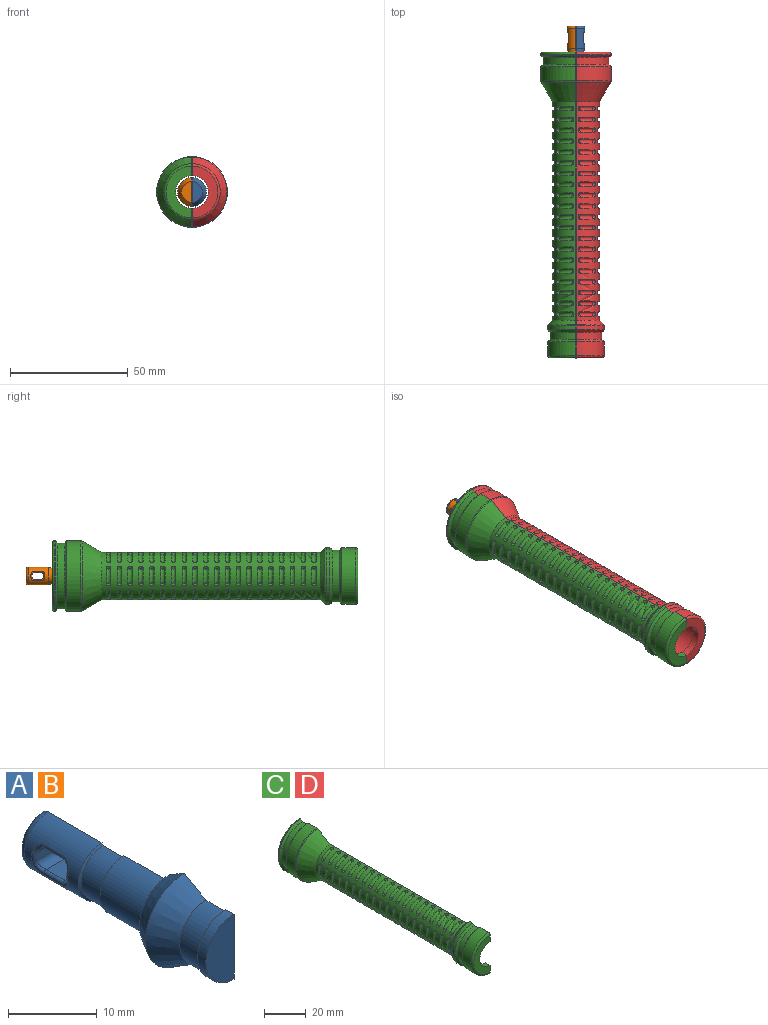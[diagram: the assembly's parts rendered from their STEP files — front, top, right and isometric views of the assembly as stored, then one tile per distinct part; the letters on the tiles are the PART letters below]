
ASSEMBLY  parts=4 mates=3
PART A: 31 faces, bbox 6.2x30.6x12.3 mm
  f0: cone r=3.5mm half-angle=60deg, axis (0,1,0), area 4mm2, adj f1,f12,f13
  f1: cylinder r=3.5mm len=7mm, axis (0,1,0), area 34.4mm2, adj f0,f2,f13
  f2: cone r=3.8mm half-angle=60deg, axis (0,-1,0), area 4mm2, adj f1,f3,f13
  f3: cylinder r=3.8mm len=7.6mm, axis (0,1,0), area 87mm2, adj f2,f4,f13
  f4: plane 9.6x4.8mm, normal (0,1,0), area 13.5mm2, adj f3,f5,f13
  f5: cone r=4.8mm half-angle=30deg, axis (0,-1,0), area 46.7mm2, adj f4,f6,f13
  f6: cone r=6.16mm half-angle=30deg, axis (0,1,0), area 64.5mm2, adj f5,f7,f13
  f7: cylinder r=4.17mm len=8.34mm, axis (0,1,0), area 39.3mm2, adj f6,f8,f13
  f8: cone r=4.17mm half-angle=60deg, axis (0,-1,0), area 4.9mm2, adj f7,f9,f13
  f9: cylinder r=4.48mm len=8.97mm, axis (0,1,0), area 18.3mm2, adj f8,f10,f13
  f10: plane 8.97x4.48mm, normal (0,-1,0), area 31.6mm2, adj f9,f13
  f11: plane 5.6x2.8mm, normal (0,1,0), area 12.3mm2, adj f13,f14
  f12: cylinder r=3.8mm len=8.54mm, axis (0,1,0), area 78mm2, adj f0,f13,f14,f23,f24,f25,f26,f27
  f13: plane 30.58x12.32mm, normal (1,0,0), area 237.3mm2, adj f0,f1,f2,f3,f4,f5,f6,f7
  f14: torus R=2.8mm, axis (0,1,0), area 17mm2, adj f11,f12,f13
  f15: plane 3.4x1mm, normal (0,-1,0), area 3.4mm2, adj f13,f19,f22,f27
  f16: plane 3x2.82mm, normal (0,0,-1), area 8.5mm2, adj f13,f19,f20,f30
  f17: plane 3.4x1mm, normal (0,1,0), area 3.4mm2, adj f13,f20,f21,f26
  f18: plane 3x2.82mm, normal (0,0,1), area 8.5mm2, adj f13,f21,f22,f23
  f19: cylinder r=1mm len=3.36mm, axis (-1,0,0), area 4.8mm2, adj f13,f15,f16,f29
  f20: cylinder r=1mm len=3.36mm, axis (1,0,0), area 4.8mm2, adj f13,f16,f17,f28
  f21: cylinder r=1mm len=3.36mm, axis (-1,0,0), area 4.8mm2, adj f13,f17,f18,f24
  f22: cylinder r=1mm len=3.36mm, axis (1,0,0), area 4.8mm2, adj f13,f15,f18,f25
  f23: cylinder r=0.4mm len=3mm, axis (0,1,0), area 2.6mm2, adj f12,f18,f24,f25
  f24: bspline ~1.89x1.68mm, area 1.4mm2, adj f12,f21,f23,f26
  f25: bspline ~1.89x1.68mm, area 1.4mm2, adj f12,f22,f23,f27
  f26: torus R=3.4mm, axis (0,1,0), area 0.7mm2, adj f12,f17,f24,f28
  f27: torus R=3.4mm, axis (0,1,0), area 0.7mm2, adj f12,f15,f25,f29
  f28: bspline ~1.89x1.68mm, area 1.4mm2, adj f12,f20,f26,f30
  f29: bspline ~1.89x1.68mm, area 1.4mm2, adj f12,f19,f27,f30
  f30: cylinder r=0.4mm len=3mm, axis (0,1,0), area 2.6mm2, adj f12,f16,f28,f29
PART B: same geometry as A
PART C: 333 faces, bbox 16.2x130x32.5 mm
  f0: cylinder r=14mm len=28mm, axis (0,1,0), area 131.9mm2, adj f1,f25,f26,f27
  f1: cone r=14mm half-angle=45deg, axis (0,-1,0), area 64.4mm2, adj f0,f2,f26,f27
  f2: cylinder r=15mm len=30mm, axis (0,1,0), area 281.9mm2, adj f1,f26,f27,f328
  f3: cone r=15mm half-angle=30deg, axis (0,1,0), area 380.1mm2, adj f4,f26,f27,f328
  f4: cylinder r=10mm len=92.84mm, axis (0,1,0), area 1921mm2, adj f3,f5,f26,f27,f28,f29,f31,f33
  f5: cone r=12mm half-angle=45deg, axis (0,-1,0), area 82.3mm2, adj f4,f26,f27,f329
  f6: cylinder r=12mm len=24mm, axis (0,1,0), area 63.8mm2, adj f7,f26,f27,f329
  f7: cone r=12mm half-angle=45deg, axis (0,1,0), area 51.1mm2, adj f6,f8,f26,f27
  f8: cylinder r=11mm len=22mm, axis (0,1,0), area 103.7mm2, adj f7,f9,f26,f27
  f9: cone r=11mm half-angle=45deg, axis (0,-1,0), area 51.1mm2, adj f8,f10,f26,f27
  f10: cylinder r=12mm len=24mm, axis (0,1,0), area 222.2mm2, adj f9,f26,f27,f330
  f11: plane 22x11mm, normal (0,-1,0), area 113.1mm2, adj f12,f26,f27,f330
  f12: cylinder r=7mm len=14mm, axis (0,1,0), area 66mm2, adj f11,f13,f26,f27
  f13: plane 18x9mm, normal (0,1,0), area 50.3mm2, adj f12,f14,f26,f27
  f14: cylinder r=9mm len=18mm, axis (0,1,0), area 275.9mm2, adj f13,f15,f26,f27
  f15: cone r=7mm half-angle=45deg, axis (0,-1,0), area 71.1mm2, adj f14,f16,f26,f27
  f16: cylinder r=7mm len=94.33mm, axis (0,1,0), area 2074.4mm2, adj f15,f17,f26,f27
  f17: cone r=10.2mm half-angle=19deg, axis (0,1,0), area 266.1mm2, adj f16,f18,f26,f27
  f18: cylinder r=10.2mm len=20.4mm, axis (0,1,0), area 80.1mm2, adj f17,f19,f26,f27
  f19: plane 22.4x11.2mm, normal (0,1,0), area 33.6mm2, adj f18,f20,f26,f27
  f20: cylinder r=11.2mm len=22.4mm, axis (0,1,0), area 249.8mm2, adj f19,f21,f26,f27
  f21: plane 22.4x11.2mm, normal (0,-1,0), area 33.6mm2, adj f20,f22,f26,f27
  f22: cylinder r=10.2mm len=20.4mm, axis (0,1,0), area 32mm2, adj f21,f26,f27,f331
  f23: plane 28x14mm, normal (0,1,0), area 110.8mm2, adj f26,f27,f331,f332
  f24: cylinder r=15mm len=30mm, axis (0,1,0), area 11.8mm2, adj f25,f26,f27,f332
  f25: cone r=15mm half-angle=45deg, axis (0,1,0), area 64.4mm2, adj f0,f24,f26,f27
  f26: plane 130x8mm, normal (1,0,0), area 414.8mm2, adj f0,f1,f2,f3,f4,f5,f6,f7
  f27: plane 130x8mm, normal (1,0,0), area 414.8mm2, adj f0,f1,f2,f3,f4,f5,f6,f7
  f28: cylinder r=1mm len=2mm, axis (0.82,0,-0.57), area 0.1mm2, adj f4,f30
  f29: cylinder r=1mm len=2mm, axis (-0.09,0,1), area 0.1mm2, adj f4,f32
  f30: sphere r=1mm, area 2.9mm2, adj f28,f31
  f31: torus R=10mm, axis (0,1,0), area 19.8mm2, adj f4,f30,f32
  f32: sphere r=1mm, area 2.9mm2, adj f29,f31
  f33: cylinder r=1mm len=2mm, axis (0.82,0,-0.57), area 0.1mm2, adj f4,f35
  f34: cylinder r=1mm len=2mm, axis (-0.09,0,1), area 0.1mm2, adj f4,f37
  f35: sphere r=1mm, area 2.9mm2, adj f33,f36
  f36: torus R=10mm, axis (0,1,0), area 19.8mm2, adj f4,f35,f37
  f37: sphere r=1mm, area 2.9mm2, adj f34,f36
  f38: cylinder r=1mm len=2mm, axis (0.82,0,-0.57), area 0.1mm2, adj f4,f40
  f39: cylinder r=1mm len=2mm, axis (-0.09,0,1), area 0.1mm2, adj f4,f42
  f40: sphere r=1mm, area 2.9mm2, adj f38,f41
  f41: torus R=10mm, axis (0,1,0), area 19.8mm2, adj f4,f40,f42
  f42: sphere r=1mm, area 2.9mm2, adj f39,f41
  f43: cylinder r=1mm len=2mm, axis (0.82,0,-0.57), area 0.1mm2, adj f4,f45
  f44: cylinder r=1mm len=2mm, axis (-0.09,0,1), area 0.1mm2, adj f4,f47
  f45: sphere r=1mm, area 2.9mm2, adj f43,f46
  f46: torus R=10mm, axis (0,1,0), area 19.8mm2, adj f4,f45,f47
  f47: sphere r=1mm, area 2.9mm2, adj f44,f46
  f48: cylinder r=1mm len=2mm, axis (0.82,0,-0.57), area 0.1mm2, adj f4,f50
  f49: cylinder r=1mm len=2mm, axis (-0.09,0,1), area 0.1mm2, adj f4,f52
  f50: sphere r=1mm, area 2.9mm2, adj f48,f51
  f51: torus R=10mm, axis (0,1,0), area 19.8mm2, adj f4,f50,f52
  f52: sphere r=1mm, area 2.9mm2, adj f49,f51
  f53: cylinder r=1mm len=2mm, axis (0.82,0,-0.57), area 0.1mm2, adj f4,f55
  f54: cylinder r=1mm len=2mm, axis (-0.09,0,1), area 0.1mm2, adj f4,f57
  f55: sphere r=1mm, area 2.9mm2, adj f53,f56
  f56: torus R=10mm, axis (0,1,0), area 19.8mm2, adj f4,f55,f57
  f57: sphere r=1mm, area 2.9mm2, adj f54,f56
  f58: cylinder r=1mm len=2mm, axis (0.82,0,-0.57), area 0.1mm2, adj f4,f60
  f59: cylinder r=1mm len=2mm, axis (-0.09,0,1), area 0.1mm2, adj f4,f62
  f60: sphere r=1mm, area 2.9mm2, adj f58,f61
  f61: torus R=10mm, axis (0,1,0), area 19.8mm2, adj f4,f60,f62
  f62: sphere r=1mm, area 2.9mm2, adj f59,f61
  f63: cylinder r=1mm len=2mm, axis (0.82,0,-0.57), area 0.1mm2, adj f4,f65
  f64: cylinder r=1mm len=2mm, axis (-0.09,0,1), area 0.1mm2, adj f4,f67
  f65: sphere r=1mm, area 2.9mm2, adj f63,f66
  f66: torus R=10mm, axis (0,1,0), area 19.8mm2, adj f4,f65,f67
  f67: sphere r=1mm, area 2.9mm2, adj f64,f66
  f68: cylinder r=1mm len=2mm, axis (0.82,0,-0.57), area 0.1mm2, adj f4,f70
  f69: cylinder r=1mm len=2mm, axis (-0.09,0,1), area 0.1mm2, adj f4,f72
  f70: sphere r=1mm, area 2.9mm2, adj f68,f71
  f71: torus R=10mm, axis (0,1,0), area 19.8mm2, adj f4,f70,f72
  f72: sphere r=1mm, area 2.9mm2, adj f69,f71
  f73: cylinder r=1mm len=2mm, axis (0.82,0,-0.57), area 0.1mm2, adj f4,f75
  f74: cylinder r=1mm len=2mm, axis (-0.09,0,1), area 0.1mm2, adj f4,f77
  f75: sphere r=1mm, area 2.9mm2, adj f73,f76
  f76: torus R=10mm, axis (0,1,0), area 19.8mm2, adj f4,f75,f77
  f77: sphere r=1mm, area 2.9mm2, adj f74,f76
  f78: cylinder r=1mm len=2mm, axis (0.82,0,-0.57), area 0.1mm2, adj f4,f80
  f79: cylinder r=1mm len=2mm, axis (-0.09,0,1), area 0.1mm2, adj f4,f82
  f80: sphere r=1mm, area 2.9mm2, adj f78,f81
  f81: torus R=10mm, axis (0,1,0), area 19.8mm2, adj f4,f80,f82
  f82: sphere r=1mm, area 2.9mm2, adj f79,f81
  f83: cylinder r=1mm len=2mm, axis (0.82,0,-0.57), area 0.1mm2, adj f4,f85
  f84: cylinder r=1mm len=2mm, axis (-0.09,0,1), area 0.1mm2, adj f4,f87
  f85: sphere r=1mm, area 2.9mm2, adj f83,f86
  f86: torus R=10mm, axis (0,1,0), area 19.8mm2, adj f4,f85,f87
  f87: sphere r=1mm, area 2.9mm2, adj f84,f86
  f88: cylinder r=1mm len=2mm, axis (0.82,0,-0.57), area 0.1mm2, adj f4,f90
  f89: cylinder r=1mm len=2mm, axis (-0.09,0,1), area 0.1mm2, adj f4,f92
  f90: sphere r=1mm, area 2.9mm2, adj f88,f91
  f91: torus R=10mm, axis (0,1,0), area 19.8mm2, adj f4,f90,f92
  f92: sphere r=1mm, area 2.9mm2, adj f89,f91
  f93: cylinder r=1mm len=2mm, axis (0.82,0,-0.57), area 0.1mm2, adj f4,f95
  f94: cylinder r=1mm len=2mm, axis (-0.09,0,1), area 0.1mm2, adj f4,f97
  f95: sphere r=1mm, area 2.9mm2, adj f93,f96
  f96: torus R=10mm, axis (0,1,0), area 19.8mm2, adj f4,f95,f97
  f97: sphere r=1mm, area 2.9mm2, adj f94,f96
  f98: cylinder r=1mm len=2mm, axis (0.82,0,-0.57), area 0.1mm2, adj f4,f100
  f99: cylinder r=1mm len=2mm, axis (-0.09,0,1), area 0.1mm2, adj f4,f102
  f100: sphere r=1mm, area 2.9mm2, adj f98,f101
  f101: torus R=10mm, axis (0,1,0), area 19.8mm2, adj f4,f100,f102
  f102: sphere r=1mm, area 2.9mm2, adj f99,f101
  f103: cylinder r=1mm len=2mm, axis (0.82,0,-0.57), area 0.1mm2, adj f4,f105
  f104: cylinder r=1mm len=2mm, axis (-0.09,0,1), area 0.1mm2, adj f4,f107
  f105: sphere r=1mm, area 2.9mm2, adj f103,f106
  f106: torus R=10mm, axis (0,1,0), area 19.8mm2, adj f4,f105,f107
  f107: sphere r=1mm, area 2.9mm2, adj f104,f106
  f108: cylinder r=1mm len=2mm, axis (0.82,0,-0.57), area 0.1mm2, adj f4,f110
  f109: cylinder r=1mm len=2mm, axis (-0.09,0,1), area 0.1mm2, adj f4,f112
  f110: sphere r=1mm, area 2.9mm2, adj f108,f111
  f111: torus R=10mm, axis (0,1,0), area 19.8mm2, adj f4,f110,f112
  f112: sphere r=1mm, area 2.9mm2, adj f109,f111
  f113: cylinder r=1mm len=2mm, axis (0.82,0,-0.57), area 0.1mm2, adj f4,f115
  f114: cylinder r=1mm len=2mm, axis (-0.09,0,1), area 0.1mm2, adj f4,f117
  f115: sphere r=1mm, area 2.9mm2, adj f113,f116
  f116: torus R=10mm, axis (0,1,0), area 19.8mm2, adj f4,f115,f117
  f117: sphere r=1mm, area 2.9mm2, adj f114,f116
  f118: cylinder r=1mm len=2mm, axis (0.82,0,-0.57), area 0.1mm2, adj f4,f120
  f119: cylinder r=1mm len=2mm, axis (-0.09,0,1), area 0.1mm2, adj f4,f122
  f120: sphere r=1mm, area 2.9mm2, adj f118,f121
  f121: torus R=10mm, axis (0,1,0), area 19.8mm2, adj f4,f120,f122
  f122: sphere r=1mm, area 2.9mm2, adj f119,f121
  f123: cylinder r=1mm len=2mm, axis (0.82,0,-0.57), area 0.1mm2, adj f4,f125
  f124: cylinder r=1mm len=2mm, axis (-0.09,0,1), area 0.1mm2, adj f4,f127
  f125: sphere r=1mm, area 2.9mm2, adj f123,f126
  f126: torus R=10mm, axis (0,1,0), area 19.8mm2, adj f4,f125,f127
  f127: sphere r=1mm, area 2.9mm2, adj f124,f126
  f128: cylinder r=1mm len=2mm, axis (0.91,0,0.42), area 0.1mm2, adj f4,f130
  f129: cylinder r=1mm len=2mm, axis (-0.91,0,0.42), area 0.1mm2, adj f4,f132
  f130: sphere r=1mm, area 2.9mm2, adj f128,f131
  f131: torus R=10mm, axis (0,1,0), area 19.8mm2, adj f4,f130,f132
  f132: sphere r=1mm, area 2.9mm2, adj f129,f131
  f133: cylinder r=1mm len=2mm, axis (0.91,0,0.42), area 0.1mm2, adj f4,f135
  f134: cylinder r=1mm len=2mm, axis (-0.91,0,0.42), area 0.1mm2, adj f4,f137
  f135: sphere r=1mm, area 2.9mm2, adj f133,f136
  f136: torus R=10mm, axis (0,1,0), area 19.8mm2, adj f4,f135,f137
  f137: sphere r=1mm, area 2.9mm2, adj f134,f136
  f138: cylinder r=1mm len=2mm, axis (0.91,0,0.42), area 0.1mm2, adj f4,f140
  f139: cylinder r=1mm len=2mm, axis (-0.91,0,0.42), area 0.1mm2, adj f4,f142
  f140: sphere r=1mm, area 2.9mm2, adj f138,f141
  f141: torus R=10mm, axis (0,1,0), area 19.8mm2, adj f4,f140,f142
  f142: sphere r=1mm, area 2.9mm2, adj f139,f141
  f143: cylinder r=1mm len=2mm, axis (0.91,0,0.42), area 0.1mm2, adj f4,f145
  f144: cylinder r=1mm len=2mm, axis (-0.91,0,0.42), area 0.1mm2, adj f4,f147
  f145: sphere r=1mm, area 2.9mm2, adj f143,f146
  f146: torus R=10mm, axis (0,1,0), area 19.8mm2, adj f4,f145,f147
  f147: sphere r=1mm, area 2.9mm2, adj f144,f146
  f148: cylinder r=1mm len=2mm, axis (0.09,0,1), area 0.1mm2, adj f4,f150
  f149: cylinder r=1mm len=2mm, axis (-0.82,0,-0.57), area 0.1mm2, adj f4,f152
  f150: sphere r=1mm, area 2.9mm2, adj f148,f151
  f151: torus R=10mm, axis (0,1,0), area 19.8mm2, adj f4,f150,f152
  f152: sphere r=1mm, area 2.9mm2, adj f149,f151
  f153: cylinder r=1mm len=2mm, axis (0.09,0,1), area 0.1mm2, adj f4,f155
  f154: cylinder r=1mm len=2mm, axis (-0.82,0,-0.57), area 0.1mm2, adj f4,f157
  f155: sphere r=1mm, area 2.9mm2, adj f153,f156
  f156: torus R=10mm, axis (0,1,0), area 19.8mm2, adj f4,f155,f157
  f157: sphere r=1mm, area 2.9mm2, adj f154,f156
  f158: cylinder r=1mm len=2mm, axis (0.09,0,1), area 0.1mm2, adj f4,f160
  f159: cylinder r=1mm len=2mm, axis (-0.82,0,-0.57), area 0.1mm2, adj f4,f162
  f160: sphere r=1mm, area 2.9mm2, adj f158,f161
  f161: torus R=10mm, axis (0,1,0), area 19.8mm2, adj f4,f160,f162
  f162: sphere r=1mm, area 2.9mm2, adj f159,f161
  f163: cylinder r=1mm len=2mm, axis (0.09,0,1), area 0.1mm2, adj f4,f165
  f164: cylinder r=1mm len=2mm, axis (-0.82,0,-0.57), area 0.1mm2, adj f4,f167
  f165: sphere r=1mm, area 2.9mm2, adj f163,f166
  f166: torus R=10mm, axis (0,1,0), area 19.8mm2, adj f4,f165,f167
  f167: sphere r=1mm, area 2.9mm2, adj f164,f166
  f168: cylinder r=1mm len=2mm, axis (0.09,0,1), area 0.1mm2, adj f4,f170
  f169: cylinder r=1mm len=2mm, axis (-0.82,0,-0.57), area 0.1mm2, adj f4,f172
  f170: sphere r=1mm, area 2.9mm2, adj f168,f171
  f171: torus R=10mm, axis (0,1,0), area 19.8mm2, adj f4,f170,f172
  f172: sphere r=1mm, area 2.9mm2, adj f169,f171
  f173: cylinder r=1mm len=2mm, axis (0.09,0,1), area 0.1mm2, adj f4,f175
  f174: cylinder r=1mm len=2mm, axis (-0.82,0,-0.57), area 0.1mm2, adj f4,f177
  f175: sphere r=1mm, area 2.9mm2, adj f173,f176
  f176: torus R=10mm, axis (0,1,0), area 19.8mm2, adj f4,f175,f177
  f177: sphere r=1mm, area 2.9mm2, adj f174,f176
  f178: cylinder r=1mm len=2mm, axis (0.09,0,1), area 0.1mm2, adj f4,f180
  f179: cylinder r=1mm len=2mm, axis (-0.82,0,-0.57), area 0.1mm2, adj f4,f182
  f180: sphere r=1mm, area 2.9mm2, adj f178,f181
  f181: torus R=10mm, axis (0,1,0), area 19.8mm2, adj f4,f180,f182
  f182: sphere r=1mm, area 2.9mm2, adj f179,f181
  f183: cylinder r=1mm len=2mm, axis (0.09,0,1), area 0.1mm2, adj f4,f185
  f184: cylinder r=1mm len=2mm, axis (-0.82,0,-0.57), area 0.1mm2, adj f4,f187
  f185: sphere r=1mm, area 2.9mm2, adj f183,f186
  f186: torus R=10mm, axis (0,1,0), area 19.8mm2, adj f4,f185,f187
  f187: sphere r=1mm, area 2.9mm2, adj f184,f186
  f188: cylinder r=1mm len=2mm, axis (0.09,0,1), area 0.1mm2, adj f4,f190
  f189: cylinder r=1mm len=2mm, axis (-0.82,0,-0.57), area 0.1mm2, adj f4,f192
  f190: sphere r=1mm, area 2.9mm2, adj f188,f191
  f191: torus R=10mm, axis (0,1,0), area 19.8mm2, adj f4,f190,f192
  f192: sphere r=1mm, area 2.9mm2, adj f189,f191
  f193: cylinder r=1mm len=2mm, axis (0.09,0,1), area 0.1mm2, adj f4,f195
  f194: cylinder r=1mm len=2mm, axis (-0.82,0,-0.57), area 0.1mm2, adj f4,f197
  f195: sphere r=1mm, area 2.9mm2, adj f193,f196
  f196: torus R=10mm, axis (0,1,0), area 19.8mm2, adj f4,f195,f197
  f197: sphere r=1mm, area 2.9mm2, adj f194,f196
  f198: cylinder r=1mm len=2mm, axis (0.09,0,1), area 0.1mm2, adj f4,f200
  f199: cylinder r=1mm len=2mm, axis (-0.82,0,-0.57), area 0.1mm2, adj f4,f202
  f200: sphere r=1mm, area 2.9mm2, adj f198,f201
  f201: torus R=10mm, axis (0,1,0), area 19.8mm2, adj f4,f200,f202
  f202: sphere r=1mm, area 2.9mm2, adj f199,f201
  f203: cylinder r=1mm len=2mm, axis (0.09,0,1), area 0.1mm2, adj f4,f205
  f204: cylinder r=1mm len=2mm, axis (-0.82,0,-0.57), area 0.1mm2, adj f4,f207
  f205: sphere r=1mm, area 2.9mm2, adj f203,f206
  f206: torus R=10mm, axis (0,1,0), area 19.8mm2, adj f4,f205,f207
  f207: sphere r=1mm, area 2.9mm2, adj f204,f206
  f208: cylinder r=1mm len=2mm, axis (0.91,0,0.42), area 0.1mm2, adj f4,f210
  f209: cylinder r=1mm len=2mm, axis (-0.91,0,0.42), area 0.1mm2, adj f4,f212
  f210: sphere r=1mm, area 2.9mm2, adj f208,f211
  f211: torus R=10mm, axis (0,1,0), area 19.8mm2, adj f4,f210,f212
  f212: sphere r=1mm, area 2.9mm2, adj f209,f211
  f213: cylinder r=1mm len=2mm, axis (0.91,0,0.42), area 0.1mm2, adj f4,f215
  f214: cylinder r=1mm len=2mm, axis (-0.91,0,0.42), area 0.1mm2, adj f4,f217
  f215: sphere r=1mm, area 2.9mm2, adj f213,f216
  f216: torus R=10mm, axis (0,1,0), area 19.8mm2, adj f4,f215,f217
  f217: sphere r=1mm, area 2.9mm2, adj f214,f216
  f218: cylinder r=1mm len=2mm, axis (0.91,0,0.42), area 0.1mm2, adj f4,f220
  f219: cylinder r=1mm len=2mm, axis (-0.91,0,0.42), area 0.1mm2, adj f4,f222
  f220: sphere r=1mm, area 2.9mm2, adj f218,f221
  f221: torus R=10mm, axis (0,1,0), area 19.8mm2, adj f4,f220,f222
  f222: sphere r=1mm, area 2.9mm2, adj f219,f221
  f223: cylinder r=1mm len=2mm, axis (0.91,0,0.42), area 0.1mm2, adj f4,f225
  f224: cylinder r=1mm len=2mm, axis (-0.91,0,0.42), area 0.1mm2, adj f4,f227
  f225: sphere r=1mm, area 2.9mm2, adj f223,f226
  f226: torus R=10mm, axis (0,1,0), area 19.8mm2, adj f4,f225,f227
  f227: sphere r=1mm, area 2.9mm2, adj f224,f226
  f228: cylinder r=1mm len=2mm, axis (0.91,0,0.42), area 0.1mm2, adj f4,f230
  f229: cylinder r=1mm len=2mm, axis (-0.91,0,0.42), area 0.1mm2, adj f4,f232
  f230: sphere r=1mm, area 2.9mm2, adj f228,f231
  f231: torus R=10mm, axis (0,1,0), area 19.8mm2, adj f4,f230,f232
  f232: sphere r=1mm, area 2.9mm2, adj f229,f231
  f233: cylinder r=1mm len=2mm, axis (0.91,0,0.42), area 0.1mm2, adj f4,f235
  f234: cylinder r=1mm len=2mm, axis (-0.91,0,0.42), area 0.1mm2, adj f4,f237
  f235: sphere r=1mm, area 2.9mm2, adj f233,f236
  f236: torus R=10mm, axis (0,1,0), area 19.8mm2, adj f4,f235,f237
  f237: sphere r=1mm, area 2.9mm2, adj f234,f236
  f238: cylinder r=1mm len=2mm, axis (0.91,0,0.42), area 0.1mm2, adj f4,f240
  f239: cylinder r=1mm len=2mm, axis (-0.91,0,0.42), area 0.1mm2, adj f4,f242
  f240: sphere r=1mm, area 2.9mm2, adj f238,f241
  f241: torus R=10mm, axis (0,1,0), area 19.8mm2, adj f4,f240,f242
  f242: sphere r=1mm, area 2.9mm2, adj f239,f241
  f243: cylinder r=1mm len=2mm, axis (0.91,0,0.42), area 0.1mm2, adj f4,f245
  f244: cylinder r=1mm len=2mm, axis (-0.91,0,0.42), area 0.1mm2, adj f4,f247
  f245: sphere r=1mm, area 2.9mm2, adj f243,f246
  f246: torus R=10mm, axis (0,1,0), area 19.8mm2, adj f4,f245,f247
  f247: sphere r=1mm, area 2.9mm2, adj f244,f246
  f248: cylinder r=1mm len=2mm, axis (0.91,0,0.42), area 0.1mm2, adj f4,f250
  f249: cylinder r=1mm len=2mm, axis (-0.91,0,0.42), area 0.1mm2, adj f4,f252
  f250: sphere r=1mm, area 2.9mm2, adj f248,f251
  f251: torus R=10mm, axis (0,1,0), area 19.8mm2, adj f4,f250,f252
  f252: sphere r=1mm, area 2.9mm2, adj f249,f251
  f253: cylinder r=1mm len=2mm, axis (0.91,0,0.42), area 0.1mm2, adj f4,f255
  f254: cylinder r=1mm len=2mm, axis (-0.91,0,0.42), area 0.1mm2, adj f4,f257
  f255: sphere r=1mm, area 2.9mm2, adj f253,f256
  f256: torus R=10mm, axis (0,1,0), area 19.8mm2, adj f4,f255,f257
  f257: sphere r=1mm, area 2.9mm2, adj f254,f256
  f258: cylinder r=1mm len=2mm, axis (0.91,0,0.42), area 0.1mm2, adj f4,f260
  f259: cylinder r=1mm len=2mm, axis (-0.91,0,0.42), area 0.1mm2, adj f4,f262
  f260: sphere r=1mm, area 2.9mm2, adj f258,f261
  f261: torus R=10mm, axis (0,1,0), area 19.8mm2, adj f4,f260,f262
  f262: sphere r=1mm, area 2.9mm2, adj f259,f261
  f263: cylinder r=1mm len=2mm, axis (0.91,0,0.42), area 0.1mm2, adj f4,f265
  f264: cylinder r=1mm len=2mm, axis (-0.91,0,0.42), area 0.1mm2, adj f4,f267
  f265: sphere r=1mm, area 2.9mm2, adj f263,f266
  f266: torus R=10mm, axis (0,1,0), area 19.8mm2, adj f4,f265,f267
  f267: sphere r=1mm, area 2.9mm2, adj f264,f266
  f268: cylinder r=1mm len=2mm, axis (0.91,0,0.42), area 0.1mm2, adj f4,f270
  f269: cylinder r=1mm len=2mm, axis (-0.91,0,0.42), area 0.1mm2, adj f4,f272
  f270: sphere r=1mm, area 2.9mm2, adj f268,f271
  f271: torus R=10mm, axis (0,1,0), area 19.8mm2, adj f4,f270,f272
  f272: sphere r=1mm, area 2.9mm2, adj f269,f271
  f273: cylinder r=1mm len=2mm, axis (0.91,0,0.42), area 0.1mm2, adj f4,f275
  f274: cylinder r=1mm len=2mm, axis (-0.91,0,0.42), area 0.1mm2, adj f4,f277
  f275: sphere r=1mm, area 2.9mm2, adj f273,f276
  f276: torus R=10mm, axis (0,1,0), area 19.8mm2, adj f4,f275,f277
  f277: sphere r=1mm, area 2.9mm2, adj f274,f276
  f278: cylinder r=1mm len=2mm, axis (0.91,0,0.42), area 0.1mm2, adj f4,f280
  f279: cylinder r=1mm len=2mm, axis (-0.91,0,0.42), area 0.1mm2, adj f4,f282
  f280: sphere r=1mm, area 2.9mm2, adj f278,f281
  f281: torus R=10mm, axis (0,1,0), area 19.8mm2, adj f4,f280,f282
  f282: sphere r=1mm, area 2.9mm2, adj f279,f281
  f283: cylinder r=1mm len=2mm, axis (0.91,0,0.42), area 0.1mm2, adj f4,f285
  f284: cylinder r=1mm len=2mm, axis (-0.91,0,0.42), area 0.1mm2, adj f4,f287
  f285: sphere r=1mm, area 2.9mm2, adj f283,f286
  f286: torus R=10mm, axis (0,1,0), area 19.8mm2, adj f4,f285,f287
  f287: sphere r=1mm, area 2.9mm2, adj f284,f286
  f288: cylinder r=1mm len=2mm, axis (0.09,0,1), area 0.1mm2, adj f4,f290
  f289: cylinder r=1mm len=2mm, axis (-0.82,0,-0.57), area 0.1mm2, adj f4,f292
  f290: sphere r=1mm, area 2.9mm2, adj f288,f291
  f291: torus R=10mm, axis (0,1,0), area 19.8mm2, adj f4,f290,f292
  f292: sphere r=1mm, area 2.9mm2, adj f289,f291
  f293: cylinder r=1mm len=2mm, axis (0.09,0,1), area 0.1mm2, adj f4,f295
  f294: cylinder r=1mm len=2mm, axis (-0.82,0,-0.57), area 0.1mm2, adj f4,f297
  f295: sphere r=1mm, area 2.9mm2, adj f293,f296
  f296: torus R=10mm, axis (0,1,0), area 19.8mm2, adj f4,f295,f297
  f297: sphere r=1mm, area 2.9mm2, adj f294,f296
  f298: cylinder r=1mm len=2mm, axis (0.09,0,1), area 0.1mm2, adj f4,f300
  f299: cylinder r=1mm len=2mm, axis (-0.82,0,-0.57), area 0.1mm2, adj f4,f302
  f300: sphere r=1mm, area 2.9mm2, adj f298,f301
  f301: torus R=10mm, axis (0,1,0), area 19.8mm2, adj f4,f300,f302
  f302: sphere r=1mm, area 2.9mm2, adj f299,f301
  f303: cylinder r=1mm len=2mm, axis (0.09,0,1), area 0.1mm2, adj f4,f305
  f304: cylinder r=1mm len=2mm, axis (-0.82,0,-0.57), area 0.1mm2, adj f4,f307
  f305: sphere r=1mm, area 2.9mm2, adj f303,f306
  f306: torus R=10mm, axis (0,1,0), area 19.8mm2, adj f4,f305,f307
  f307: sphere r=1mm, area 2.9mm2, adj f304,f306
  f308: cylinder r=1mm len=2mm, axis (0.09,0,1), area 0.1mm2, adj f4,f310
  f309: cylinder r=1mm len=2mm, axis (-0.82,0,-0.57), area 0.1mm2, adj f4,f312
  f310: sphere r=1mm, area 2.9mm2, adj f308,f311
  f311: torus R=10mm, axis (0,1,0), area 19.8mm2, adj f4,f310,f312
  f312: sphere r=1mm, area 2.9mm2, adj f309,f311
  f313: cylinder r=1mm len=2mm, axis (0.09,0,1), area 0.1mm2, adj f4,f315
  f314: cylinder r=1mm len=2mm, axis (-0.82,0,-0.57), area 0.1mm2, adj f4,f317
  f315: sphere r=1mm, area 2.9mm2, adj f313,f316
  f316: torus R=10mm, axis (0,1,0), area 19.8mm2, adj f4,f315,f317
  f317: sphere r=1mm, area 2.9mm2, adj f314,f316
  f318: cylinder r=1mm len=2mm, axis (0.09,0,1), area 0.1mm2, adj f4,f320
  f319: cylinder r=1mm len=2mm, axis (-0.82,0,-0.57), area 0.1mm2, adj f4,f322
  f320: sphere r=1mm, area 2.9mm2, adj f318,f321
  f321: torus R=10mm, axis (0,1,0), area 19.8mm2, adj f4,f320,f322
  f322: sphere r=1mm, area 2.9mm2, adj f319,f321
  f323: cylinder r=1mm len=2mm, axis (0.09,0,1), area 0.1mm2, adj f4,f325
  f324: cylinder r=1mm len=2mm, axis (-0.82,0,-0.57), area 0.1mm2, adj f4,f327
  f325: sphere r=1mm, area 2.9mm2, adj f323,f326
  f326: torus R=10mm, axis (0,1,0), area 19.8mm2, adj f4,f325,f327
  f327: sphere r=1mm, area 2.9mm2, adj f324,f326
  f328: torus R=14mm, axis (0,-1,0), area 24.6mm2, adj f2,f3,f26,f27
  f329: torus R=11mm, axis (0,-1,0), area 29.4mm2, adj f5,f6,f26,f27
  f330: torus R=11mm, axis (0,1,0), area 57.4mm2, adj f10,f11,f26,f27
  f331: torus R=11.2mm, axis (0,-1,0), area 52.1mm2, adj f22,f23,f26,f27
  f332: torus R=14mm, axis (0,-1,0), area 72.2mm2, adj f23,f24,f26,f27
PART D: same geometry as C
PLACE A rot(axis=(0,-1,0),180deg) t=(9.2,1.11,0)mm
PLACE B t=(0,1.11,0)mm
PLACE C at identity
PLACE D rot(axis=(0,-1,0),180deg) t=(9.2,0,0)mm
MATE fastened D.f330 <-> C.f330  axis (0,1,0) through (4.6,4.16,0)mm
MATE revolute A.f8 <-> C.f330  axis (0,1,0) through (4.6,66.69,0)mm
MATE fastened A.f13 <-> B.f13  axis (-1,0,0) through (4.6,66.6,0)mm
